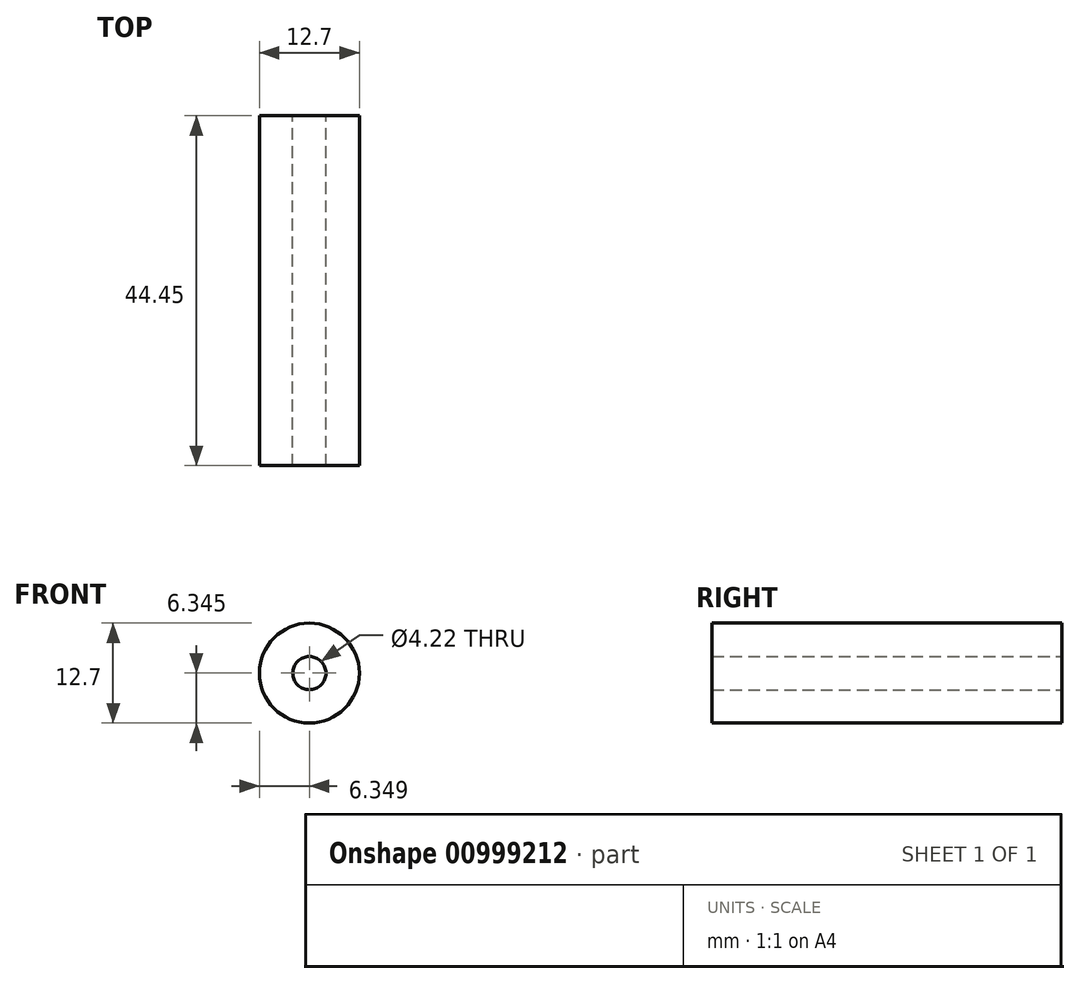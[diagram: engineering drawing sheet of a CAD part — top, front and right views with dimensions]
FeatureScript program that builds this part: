
annotation { "Feature Type Name" : "Feature", "Feature Type Description" : "" }
export const myFeature = defineFeature(function(context is Context, id is Id, definition is map)
    precondition{}
    {
        {
            var Q0;
            Q0=qCreatedBy(makeId("Front.planeOp"),FACE);
            var sketch = newSketch(context, id + "F0", { "sketchPlane" : qUnion([Q0])});
            skCircle(sketch, "E0", {"center": v(-11.35, 12.39) * mm, "radius": 2.1 * mm});
            skCircle(sketch, "E1", {"center": v(-11.35, 12.39) * mm, "radius": 6.35 * mm});
            skSolve(sketch);
        }
        {
            var Q0;
            Q0 = qSketchRegion(id + "F0", true);
            extrude(context, id + "F1", {"entities" : qUnion([Q0]), "depth" : 44.45 * mm, "offsetDistance" : 25.4 * mm});
        }
    });
